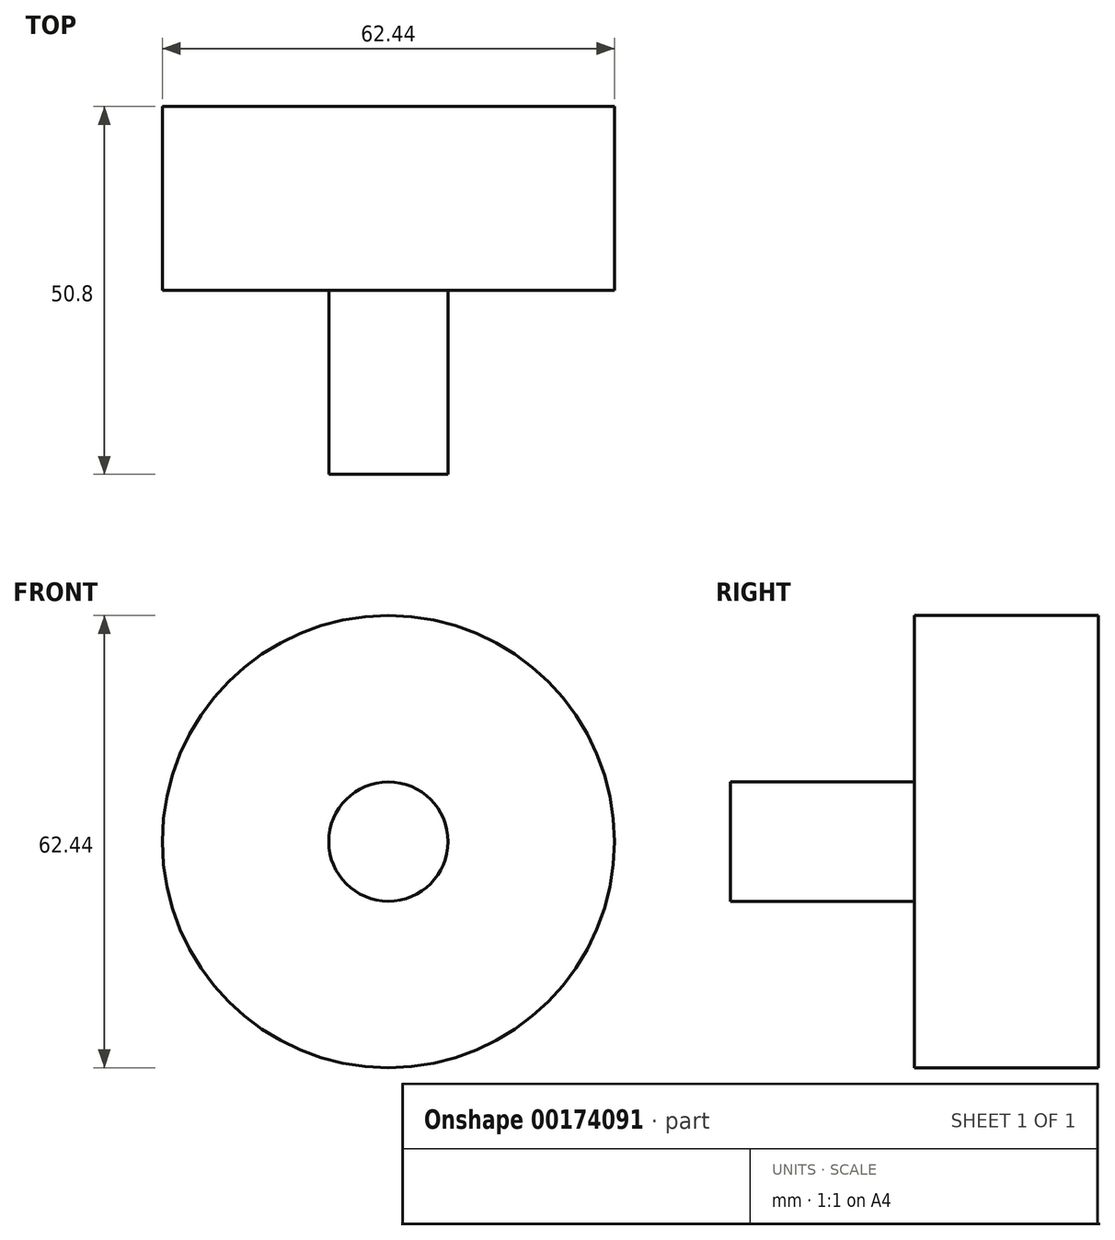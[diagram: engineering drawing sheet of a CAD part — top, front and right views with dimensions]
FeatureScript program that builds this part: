
annotation { "Feature Type Name" : "Feature", "Feature Type Description" : "" }
export const myFeature = defineFeature(function(context is Context, id is Id, definition is map)
    precondition{}
    {
        {
            var Q0;
            Q0=qCreatedBy(makeId("Front.planeOp"),FACE);
            var sketch = newSketch(context, id + "F0", { "sketchPlane" : qUnion([Q0])});
            skCircle(sketch, "E0", {"center": v(0, 0) * mm, "radius": 31.22 * mm});
            skSolve(sketch);
        }
        {
            var Q0;
            Q0 = qSketchRegion(id + "F0", true);
            extrude(context, id + "F1", {"entities" : qUnion([Q0]), "depth" : 25.4 * mm});
        }
        {
            var Q0;
            Q0=makeQuery(id+"F1.opExtrude","CAP_FACE",FACE,{"disambiguationData":[OSD([sQuery(id+"F0.wireOp",EDGE,"E0")])],"isStart":false});
            var sketch = newSketch(context, id + "F2", { "sketchPlane" : qUnion([Q0])});
            skCircle(sketch, "E1", {"center": v(0, 0) * mm, "radius": 8.23 * mm});
            skSolve(sketch);
        }
        {
            var Q0;
            Q0 = qSketchRegion(id + "F2", true);
            extrude(context, id + "F3", {"entities" : qUnion([Q0]), "operationType" : NewBodyOperationType.ADD, "depth" : 25.4 * mm});
        }
        {
            var Q0;
            Q0=makeQuery(id+"F3.opExtrude","CAP_FACE",FACE,{"disambiguationData":[OSD([sQuery(id+"F2.wireOp",EDGE,"E1")])],"isStart":false});
            extrude(context, id + "F4", {"entities" : qUnion([Q0]), "operationType" : NewBodyOperationType.ADD, "oppositeDirection" : true, "depth" : 25.4 * mm});
        }
    });
